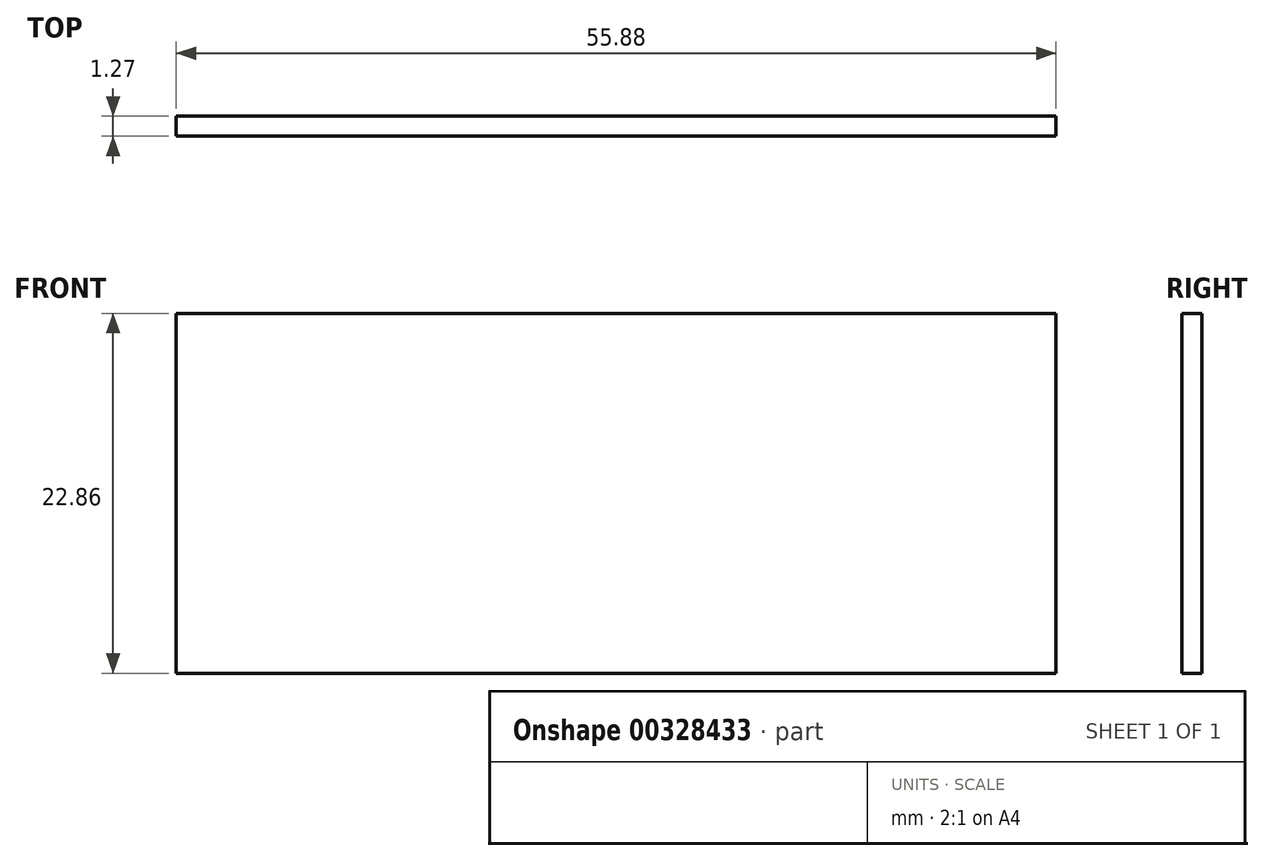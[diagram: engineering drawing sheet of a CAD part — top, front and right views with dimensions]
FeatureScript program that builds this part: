
annotation { "Feature Type Name" : "Feature", "Feature Type Description" : "" }
export const myFeature = defineFeature(function(context is Context, id is Id, definition is map)
    precondition{}
    {
        {
            var Q0;
            Q0=qCreatedBy(makeId("Front.planeOp"),FACE);
            var sketch = newSketch(context, id + "F0", { "sketchPlane" : qUnion([Q0])});
            skLineSegment(sketch, "E0.bottom", {"start": v(0, 0) * mm, "end": v(55.88, 0) * mm});
            skLineSegment(sketch, "E0.top", {"start": v(0, 22.86) * mm, "end": v(55.88, 22.86) * mm});
            skLineSegment(sketch, "E0.left", {"start": v(0, 0) * mm, "end": v(0, 22.86) * mm});
            skLineSegment(sketch, "E0.right", {"start": v(55.88, 0) * mm, "end": v(55.88, 22.86) * mm});
            skSolve(sketch);
        }
        {
            var Q0;
            Q0=makeQuery(id+"F0.imprint","IMPRINT",FACE,{"disambiguationData":[TD([[makeQuery(id+"F0.imprint","IMPRINT",EDGE,{"derivedFrom":sQuery(id+"F0.wireOp",EDGE,"E0.bottom")}),1.0]])]});
            extrude(context, id + "F1", {"entities" : qUnion([Q0]), "depth" : 1.27 * mm});
        }
    });
